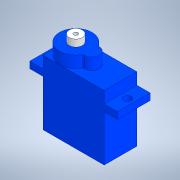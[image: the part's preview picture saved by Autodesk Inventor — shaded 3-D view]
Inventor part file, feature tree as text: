
AUTODESK INVENTOR PART (.ipt)
format: ipt  version: 2020 (Build 240168000, 168)  size: 170,496 bytes
history: native  units: mm
features: extrude x4, sketch x4
ambient origin geometry x8: Origin, YZ Plane, XZ Plane, XY Plane, X Axis, Y Axis, Z Axis, Center Point
bodies: Solid1 (feature_tree)
feature tree (8):
  extrude  "Extrusion1"  Depth=22.45mm
  extrude  "Extrusion2"  Depth=17.0mm
  extrude  "Extrusion3"  Depth=4.9mm
  extrude  "Extrusion4"  Depth=2.55mm
  sketch  "Sketch1"  dims[d0=23.75mm d1=22.45mm]
  sketch  "Sketch2"  dims[d2=2.45mm d3=17.0mm]
  sketch  "Sketch3"  dims[d4=4.9mm d5=4.9mm]
  sketch  "Sketch4"  dims[d6=12.0mm d7=0.0mm d8=2.77mm d9=27.5mm d10=10.0mm d11=0.0mm d12=5.5mm d13=14.6mm d14=4.3mm d15=0.0mm d16=4.84mm d17=1.5mm d18=2.55mm d19=0.0mm]
